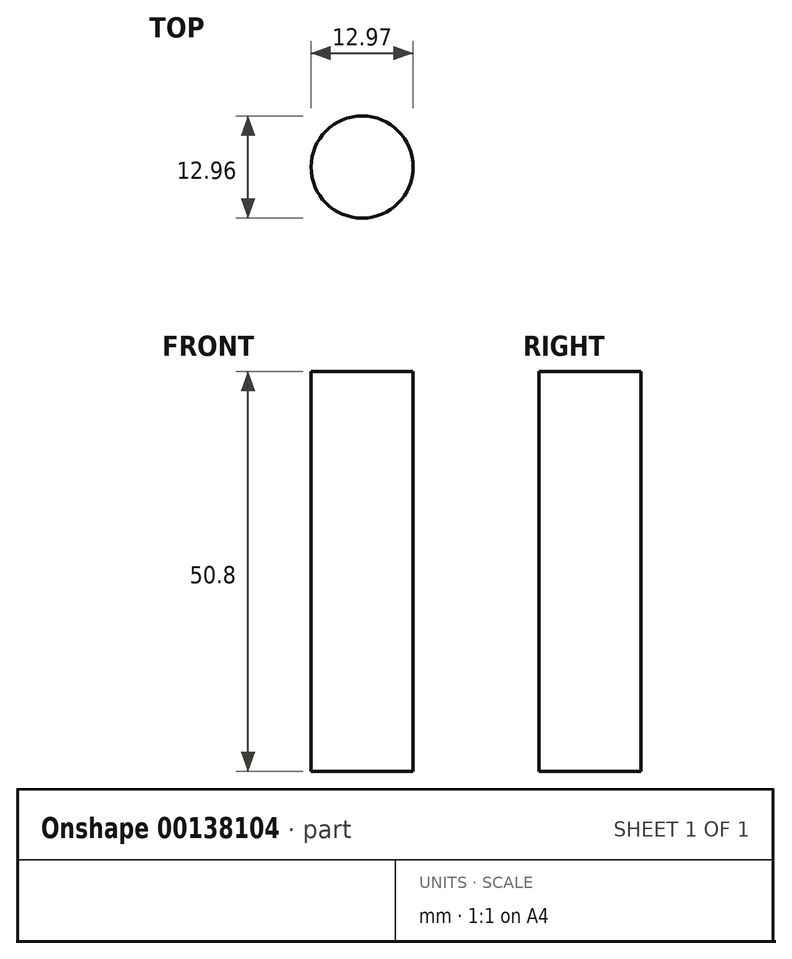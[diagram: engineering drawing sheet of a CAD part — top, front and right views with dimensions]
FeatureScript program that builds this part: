
annotation { "Feature Type Name" : "Feature", "Feature Type Description" : "" }
export const myFeature = defineFeature(function(context is Context, id is Id, definition is map)
    precondition{}
    {
        {
            var Q0;
            Q0=qCreatedBy(makeId("Top.planeOp"),FACE);
            var sketch = newSketch(context, id + "F0", { "sketchPlane" : qUnion([Q0])});
            skCircle(sketch, "E0", {"center": v(-23.55, 23.1) * mm, "radius": 6.48 * mm});
            skSolve(sketch);
        }
        {
            var Q0;
            Q0 = qSketchRegion(id + "F0", true);
            extrude(context, id + "F1", {"entities" : qUnion([Q0]), "depth" : 50.8 * mm});
        }
    });
